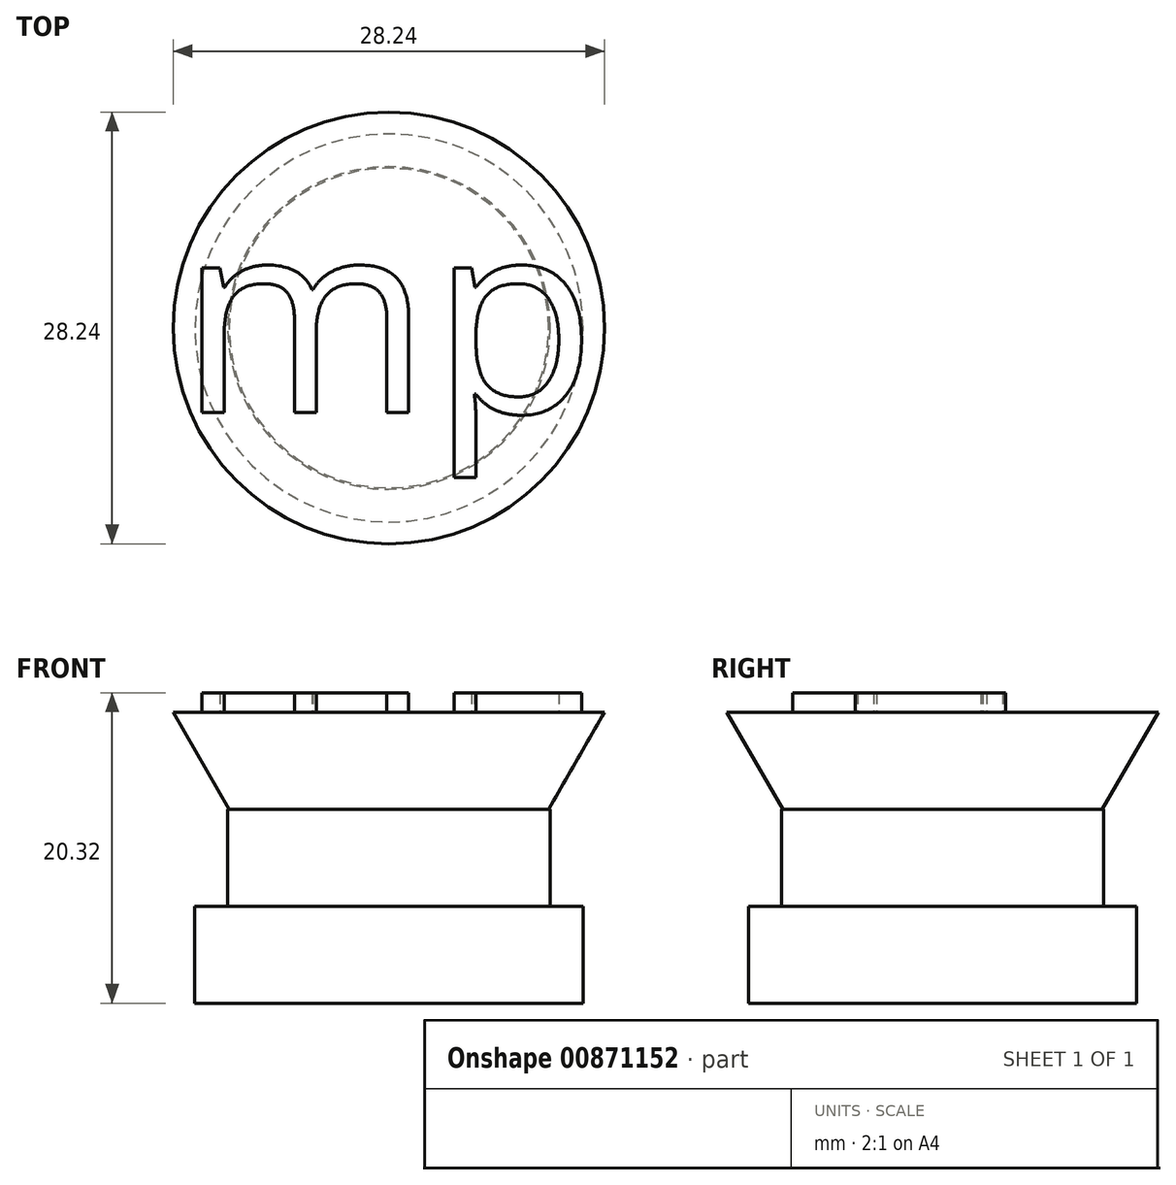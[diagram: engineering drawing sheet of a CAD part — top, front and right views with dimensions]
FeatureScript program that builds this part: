
annotation { "Feature Type Name" : "Feature", "Feature Type Description" : "" }
export const myFeature = defineFeature(function(context is Context, id is Id, definition is map)
    precondition{}
    {
        {
            var Q0;
            Q0=qCreatedBy(makeId("Top.planeOp"),FACE);
            var sketch = newSketch(context, id + "F0", { "sketchPlane" : qUnion([Q0])});
            skCircle(sketch, "E0", {"center": v(0, 0) * mm, "radius": 12.7 * mm});
            skSolve(sketch);
        }
        {
            var Q0;
            Q0=makeQuery(id+"F0.imprint","IMPRINT",FACE,{"disambiguationData":[TD([[makeQuery(id+"F0.imprint","IMPRINT",EDGE,{"derivedFrom":sQuery(id+"F0.wireOp",EDGE,"E0")}),1.0]])]});
            extrude(context, id + "F1", {"entities" : qUnion([Q0]), "depth" : 6.35 * mm, "offsetDistance" : 25.4 * mm});
        }
        {
            var Q0;
            Q0=makeQuery(id+"F1.opExtrude","CAP_FACE",FACE,{"disambiguationData":[OSD([sQuery(id+"F0.wireOp",EDGE,"E0")])],"isStart":false});
            var sketch = newSketch(context, id + "F2", { "sketchPlane" : qUnion([Q0])});
            skCircle(sketch, "E1", {"center": v(0, 0) * mm, "radius": 10.55 * mm});
            skSolve(sketch);
        }
        {
            var Q0;
            Q0=makeQuery(id+"F2.imprint","IMPRINT",FACE,{"disambiguationData":[TD([[makeQuery(id+"F2.imprint","IMPRINT",EDGE,{"derivedFrom":sQuery(id+"F2.wireOp",EDGE,"E1")}),1.0]])]});
            extrude(context, id + "F3", {"entities" : qUnion([Q0]), "operationType" : NewBodyOperationType.ADD, "depth" : 6.35 * mm, "offsetDistance" : 25.4 * mm});
        }
        {
            var Q0;
            Q0=makeQuery(id+"F3.opExtrude","CAP_FACE",FACE,{"disambiguationData":[OSD([sQuery(id+"F2.wireOp",EDGE,"E1")])],"isStart":false});
            var sketch = newSketch(context, id + "F4", { "sketchPlane" : qUnion([Q0])});
            skCircle(sketch, "E2", {"center": v(0, 0) * mm, "radius": 10.46 * mm});
            skCircle(sketch, "E3", {"center": v(0, 0) * mm, "radius": 10.3 * mm});
            skSolve(sketch);
        }
        {
            var Q0;
            Q0 = qSketchRegion(id + "F4", true);
            var Q1;
            Q1=makeQuery(id+"F4.imprint","IMPRINT",FACE,{"disambiguationData":[TD([[makeQuery(id+"F4.imprint","IMPRINT",EDGE,{"derivedFrom":sQuery(id+"F4.wireOp",EDGE,"E3")}),1.0]])]});
            extrude(context, id + "F5", {"entities" : qUnion([Q0, Q1]), "operationType" : NewBodyOperationType.ADD, "depth" : 6.35 * mm, "offsetDistance" : 25.4 * mm, "hasDraft" : true, "draftAngle" : 30 * degree});
        }
        {
            var Q0;
            Q0=makeQuery(id+"F5.opExtrude","CAP_FACE",FACE,{"disambiguationData":[OSD([sQuery(id+"F4.wireOp",EDGE,"E2")])],"isStart":false});
            var sketch = newSketch(context, id + "F6", { "sketchPlane" : qUnion([Q0])});
            skSolve(sketch);
        }
        {
            var Q0;
            Q0=makeQuery(id+"F6.imprint","IMPRINT",FACE,{"disambiguationData":[TD([[makeQuery(id+"F6.imprint","IMPRINT",EDGE,{"derivedFrom":makeQuery(id+"F5.opExtrude","CAP_EDGE",EDGE,{"disambiguationData":[OSD([sQuery(id+"F4.wireOp",EDGE,"E2")])],"isStart":false})}),1.0]])]});
            var sketch = newSketch(context, id + "F7", { "sketchPlane" : qUnion([Q0])});
            skText(sketch, "E4", { "text": "mp", "fontName": "OpenSans-Regular.ttf"});
            const initialGuessF7  = {"E4": [-0.01375, -0.00554, 1, 0, 0.01276]};
            skSetInitialGuess(sketch, initialGuessF7);
            skSolve(sketch);
        }
        {
            var Q0;
            Q0 = qSketchRegion(id + "F7", true);
            extrude(context, id + "F8", {"entities" : qUnion([Q0]), "operationType" : NewBodyOperationType.ADD, "depth" : 1.27 * mm, "offsetDistance" : 25.4 * mm});
        }
    });
